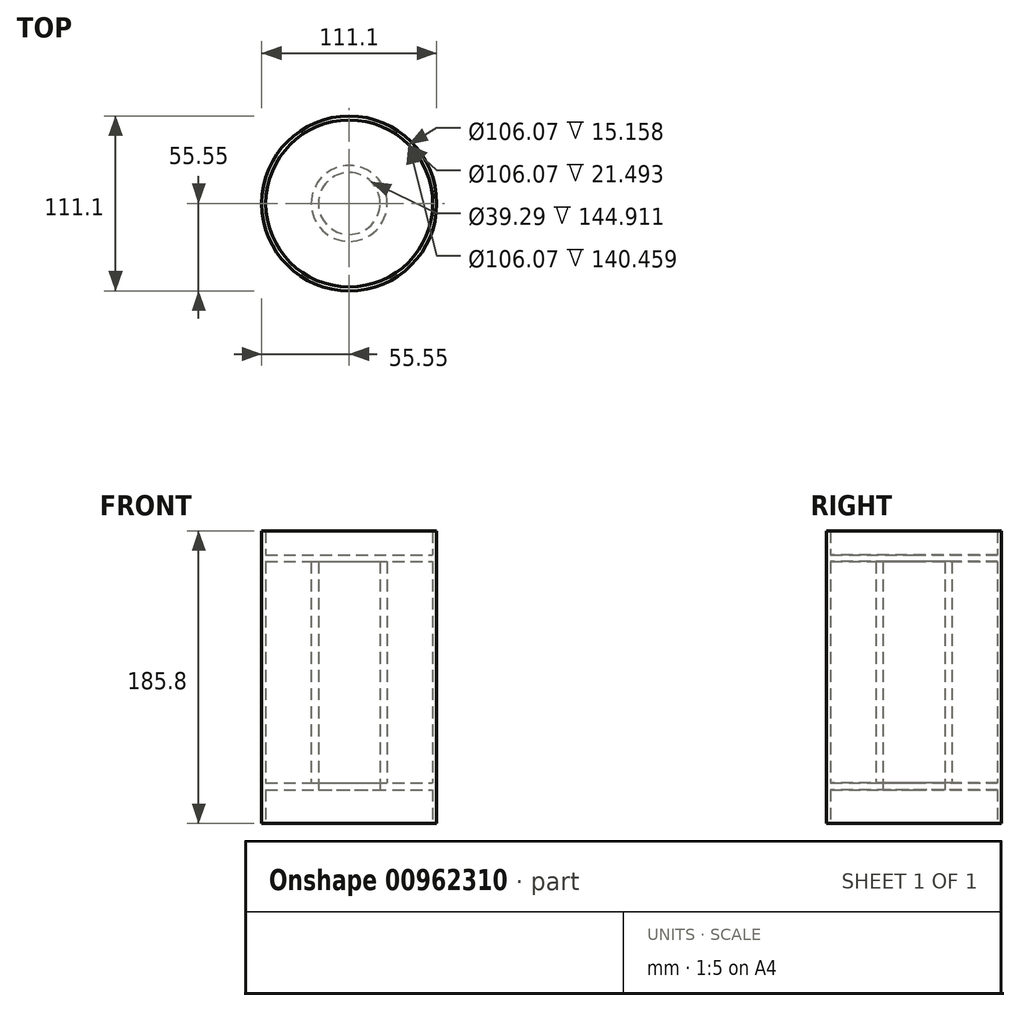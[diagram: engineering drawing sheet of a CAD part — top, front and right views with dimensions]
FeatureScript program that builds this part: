
annotation { "Feature Type Name" : "Feature", "Feature Type Description" : "" }
export const myFeature = defineFeature(function(context is Context, id is Id, definition is map)
    precondition{}
    {
        {
            var Q0;
            Q0=qCreatedBy(makeId("Front.planeOp"),FACE);
            var sketch = newSketch(context, id + "F0", { "sketchPlane" : qUnion([Q0])});
            skLineSegment(sketch, "E0", {"start": v(0, 70.86) * mm, "end": v(-38.2, 70.86) * mm});
            skLineSegment(sketch, "E1", {"start": v(-38.2, 70.86) * mm, "end": v(-38.2, 66.62) * mm});
            skLineSegment(sketch, "E2", {"start": v(-38.2, 66.62) * mm, "end": v(0, 66.62) * mm});
            skLineSegment(sketch, "E3", {"start": v(0, 66.62) * mm, "end": v(0, 70.86) * mm});
            skLineSegment(sketch, "E4", {"start": v(-38.2, 70.86) * mm, "end": v(-53.04, 70.86) * mm});
            skLineSegment(sketch, "E5", {"start": v(-53.04, 70.86) * mm, "end": v(-53.04, 66.62) * mm});
            skLineSegment(sketch, "E6", {"start": v(-53.04, 66.62) * mm, "end": v(-38.2, 66.62) * mm});
            skLineSegment(sketch, "E7", {"start": v(-53.04, 70.86) * mm, "end": v(-53.04, 86.02) * mm});
            skLineSegment(sketch, "E8", {"start": v(-53.04, 86.02) * mm, "end": v(-55.55, 86.02) * mm});
            skLineSegment(sketch, "E9", {"start": v(-55.55, 86.02) * mm, "end": v(-55.55, -99.78) * mm});
            skLineSegment(sketch, "E10", {"start": v(-55.55, -99.78) * mm, "end": v(-53.04, -99.78) * mm});
            skLineSegment(sketch, "E11", {"start": v(-53.04, -99.78) * mm, "end": v(-53.04, 86.02) * mm});
            skLineSegment(sketch, "E12.bottom", {"start": v(-24.15, 66.62) * mm, "end": v(-19.64, 66.62) * mm});
            skLineSegment(sketch, "E12.top", {"start": v(-24.15, -73.84) * mm, "end": v(-19.64, -73.84) * mm});
            skLineSegment(sketch, "E12.left", {"start": v(-24.15, 66.62) * mm, "end": v(-24.15, -73.84) * mm});
            skLineSegment(sketch, "E12.right", {"start": v(-19.64, 66.62) * mm, "end": v(-19.64, -73.84) * mm});
            skLineSegment(sketch, "E13.bottom", {"start": v(-24.15, -73.84) * mm, "end": v(-53.04, -73.84) * mm});
            skLineSegment(sketch, "E13.top", {"start": v(-24.15, -69.3) * mm, "end": v(-53.04, -69.3) * mm});
            skLineSegment(sketch, "E13.left", {"start": v(-24.15, -73.84) * mm, "end": v(-24.15, -69.3) * mm});
            skLineSegment(sketch, "E13.right", {"start": v(-53.04, -73.84) * mm, "end": v(-53.04, -69.3) * mm});
            skLineSegment(sketch, "E14.bottom", {"start": v(-19.64, -73.84) * mm, "end": v(-53.04, -73.84) * mm});
            skLineSegment(sketch, "E14.top", {"start": v(-19.64, -78.3) * mm, "end": v(-53.04, -78.3) * mm});
            skLineSegment(sketch, "E14.left", {"start": v(-19.64, -73.84) * mm, "end": v(-19.64, -78.3) * mm});
            skLineSegment(sketch, "E14.right", {"start": v(-53.04, -73.84) * mm, "end": v(-53.04, -78.3) * mm});
            skLineSegment(sketch, "E15.bottom", {"start": v(0, 70.86) * mm, "end": v(-2.2, 70.86) * mm});
            skLineSegment(sketch, "E15.top", {"start": v(0, 66.62) * mm, "end": v(-2.2, 66.62) * mm});
            skLineSegment(sketch, "E15.left", {"start": v(0, 70.86) * mm, "end": v(0, 66.62) * mm});
            skLineSegment(sketch, "E15.right", {"start": v(-2.2, 70.86) * mm, "end": v(-2.2, 66.62) * mm});
            skSolve(sketch);
        }
        {
            var Q0;
            Q0 = qSketchRegion(id + "F0", true);
            var Q1;
            Q1=sQuery(id+"F0.wireOp",EDGE,"E3");
            revolve(context, id + "F1", {"surfaceOperationType" : NewSurfaceOperationType.NEW, "entities" : qUnion([Q0]), "axis" : qUnion([Q1]), "revolveType" : RevolveType.FULL});
        }
    });
